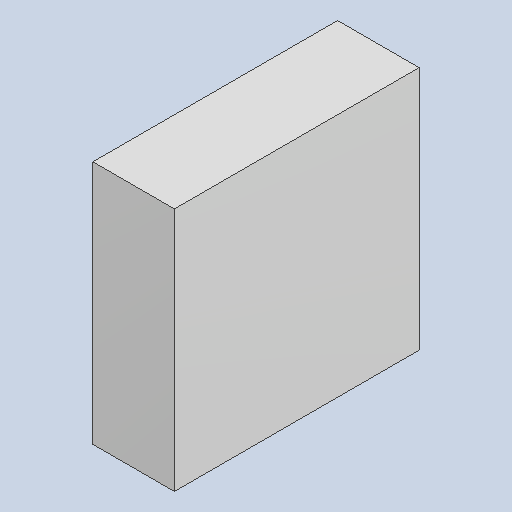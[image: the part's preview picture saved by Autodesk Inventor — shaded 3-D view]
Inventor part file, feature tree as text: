
AUTODESK INVENTOR PART (.ipt)
format: ipt  version: 2023.4 (Build 274418000, 418)  size: 81,408 bytes
history: native  units: mm
features: extrude x1
ambient origin geometry x8: Origin, YZ Plane, XZ Plane, XY Plane, X Axis, Y Axis, Z Axis, Center Point
bodies: Solid1 (feature_tree)
feature tree (1):
  extrude  "Extruded_39"  [1 undecoded]
note: 1 required parameter value undecoded (feature->parameter linkage not recoverable at this tier; creation-order binding heuristic only, values carry confidence <= 0.55)
